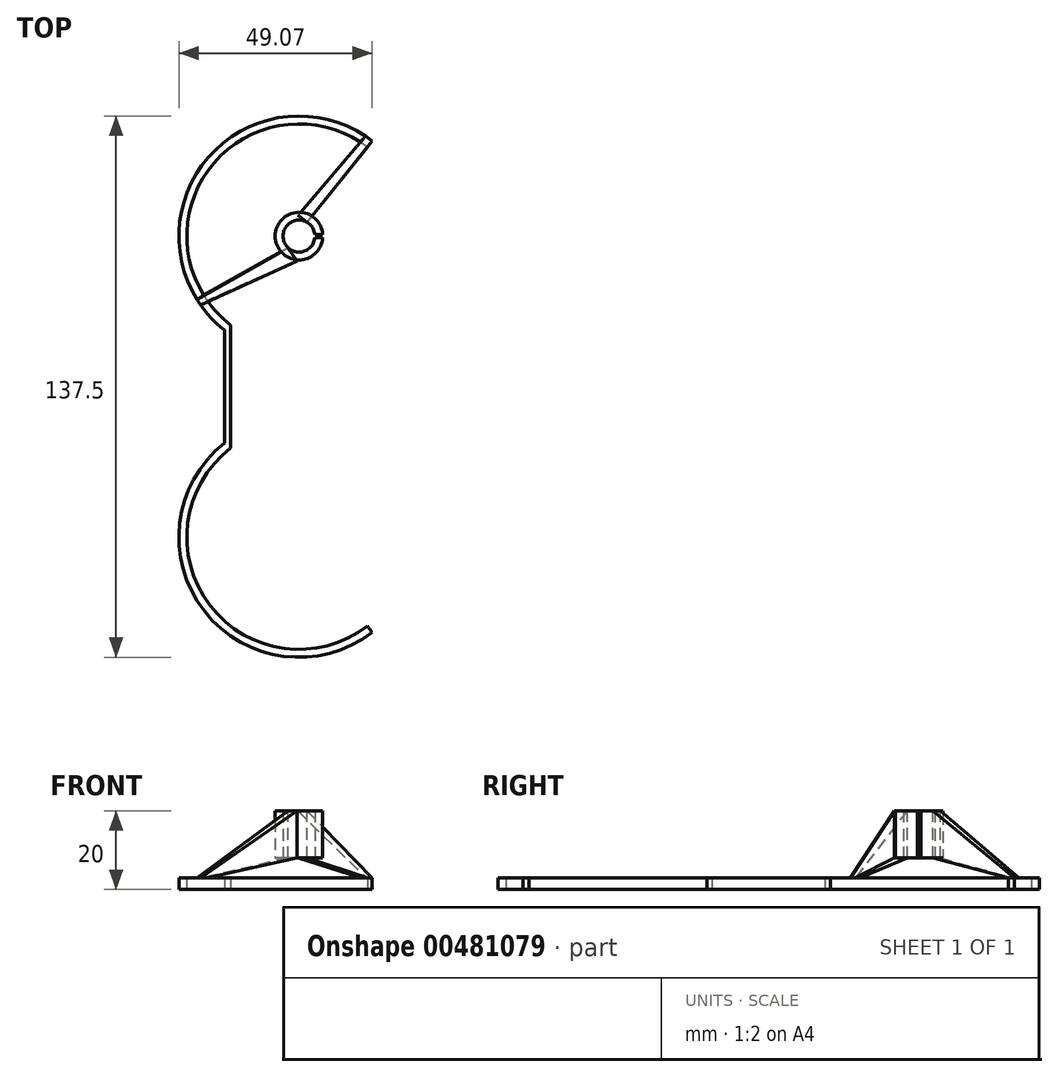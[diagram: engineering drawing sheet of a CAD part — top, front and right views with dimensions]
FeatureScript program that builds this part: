
annotation { "Feature Type Name" : "Feature", "Feature Type Description" : "" }
export const myFeature = defineFeature(function(context is Context, id is Id, definition is map)
    precondition{}
    {
        {
            var Q0;
            Q0=qCreatedBy(makeId("Top.planeOp"),FACE);
            var sketch = newSketch(context, id + "F0", { "sketchPlane" : qUnion([Q0])});
            skPoint(sketch, "E0.MirrorP", {"position": v(0, -38.25) * mm});
            skCircle(sketch, "E1", {"center": v(0, 38.25) * mm, "radius": 28.5 * mm});
            skLineSegment(sketch, "E2", {"start": v(0, 38.25) * mm, "end": v(45.61, 38.25) * mm, "construction": true});
            skCircle(sketch, "E3", {"center": v(0, 38.25) * mm, "radius": 30.5 * mm});
            skLineSegment(sketch, "E4", {"start": v(0, 38.25) * mm, "end": v(-46.13, 38.25) * mm, "construction": true});
            skLineSegment(sketch, "E5.left", {"start": v(-18.95, 14.35) * mm, "end": v(-18.95, 0) * mm});
            skLineSegment(sketch, "E5.right", {"start": v(-17.35, 13.17) * mm, "end": v(-17.35, 0) * mm});
            skLineSegment(sketch, "E6", {"start": v(-18.95, 0) * mm, "end": v(-17.35, 0) * mm});
            skLineSegment(sketch, "E7", {"start": v(-17.35, 15.64) * mm, "end": v(-17.35, 13.17) * mm});
            skLineSegment(sketch, "E8", {"start": v(-17.35, 15.64) * mm, "end": v(18.57, 62.45) * mm, "construction": true});
            skLineSegment(sketch, "E9", {"start": v(17.35, 60.86) * mm, "end": v(18.57, 62.45) * mm});
            skLineSegment(sketch, "E10", {"start": v(-24.98, 20.76) * mm, "end": v(0, 38.25) * mm, "construction": true});
            skSolve(sketch);
        }
        {
            var Q0;
            {var subQ0=sQuery(id+"F0.wireOp",EDGE,"E7");Q0=makeQuery(id+"F0.imprint","IMPRINT",FACE,{"disambiguationData":[TD([[makeQuery(id+"F0.imprint","IMPRINT",EDGE,{"derivedFrom":subQ0}),-1.0]])]});}
            var Q1;
            {var subQ0=sQuery(id+"F0.wireOp",EDGE,"E5.left");Q1=makeQuery(id+"F0.imprint","IMPRINT",FACE,{"disambiguationData":[TD([[makeQuery(id+"F0.imprint","IMPRINT",EDGE,{"derivedFrom":subQ0}),1.0]])]});}
            extrude(context, id + "F1", {"entities" : qUnion([Q0, Q1]), "offsetDistance" : 25 * mm, "depth" : 3 * mm});
        }
        {
            var Q0;
            Q0=makeQuery(id+"F1.opExtrude","CAP_FACE",FACE,{"disambiguationData":[OSD([sQuery(id+"F0.wireOp",EDGE,"E1"),sQuery(id+"F0.wireOp",EDGE,"E3"),sQuery(id+"F0.wireOp",EDGE,"E5.left"),sQuery(id+"F0.wireOp",EDGE,"E5.right"),sQuery(id+"F0.wireOp",EDGE,"E6"),sQuery(id+"F0.wireOp",EDGE,"E7"),sQuery(id+"F0.wireOp",EDGE,"E9")])],"isStart":false});
            cPlane(context, id + "F2", {"entities" : qUnion([Q0]), "cplaneType" : CPlaneType.OFFSET, "offset" : 5 * mm, "width" : 150 * mm, "height" : 150 * mm});
        }
        {
            var Q0;
            Q0=qCreatedBy(id+"F2.planeOp",FACE);
            var sketch = newSketch(context, id + "F3", { "sketchPlane" : qUnion([Q0])});
            skCircle(sketch, "E11", {"center": v(0, 38.25) * mm, "radius": 4.05 * mm});
            skCircle(sketch, "E12", {"center": v(0, 38.25) * mm, "radius": 6.05 * mm});
            skLineSegment(sketch, "E13.bottom", {"start": v(4.03, 37.85) * mm, "end": v(6.05, 37.85) * mm});
            skLineSegment(sketch, "E13.top", {"start": v(4.03, 38.65) * mm, "end": v(6.05, 38.65) * mm});
            skLineSegment(sketch, "E13.left", {"start": v(4.03, 37.85) * mm, "end": v(4.03, 38.65) * mm});
            skLineSegment(sketch, "E13.right", {"start": v(6.05, 37.85) * mm, "end": v(6.05, 38.65) * mm});
            skPoint(sketch, "E13.middle", {"position": v(5.04, 38.25) * mm});
            skLineSegment(sketch, "E14", {"start": v(-4.96, 34.78) * mm, "end": v(-3.32, 35.93) * mm, "construction": true});
            skLineSegment(sketch, "E15", {"start": v(2.47, 41.46) * mm, "end": v(3.68, 43.05) * mm, "construction": true});
            skLineSegment(sketch, "E16", {"start": v(-6.78, 40.88) * mm, "end": v(0.15, 30.98) * mm, "construction": true});
            skLineSegment(sketch, "E17", {"start": v(-1.22, 44.29) * mm, "end": v(6.15, 38.64) * mm, "construction": true});
            skSolve(sketch);
        }
        {
            var Q0;
            {var subQ4=sQuery(id+"F3.wireOp",EDGE,"E13.top");var subQ6=sQuery(id+"F3.wireOp",EDGE,"E12");var subQ8=makeQuery(id+"F3.imprint","INTERSECT",VERTEX,{"derivedFrom":[subQ6,subQ4]});Q0=makeQuery(id+"F3.imprint","IMPRINT",FACE,{"disambiguationData":[TD([[makeQuery(id+"F3.imprint","IMPRINT",EDGE,{"disambiguationData":[TD([[subQ8,-1.0]])],"derivedFrom":subQ6}),1.0]])]});}
            extrude(context, id + "F4", {"entities" : qUnion([Q0]), "depth" : 12 * mm, "offsetDistance" : 25 * mm});
        }
        {
            var Q0;
            Q0=makeQuery(id+"F1.opExtrude","CAP_FACE",FACE,{"disambiguationData":[OSD([sQuery(id+"F0.wireOp",EDGE,"E1"),sQuery(id+"F0.wireOp",EDGE,"E3"),sQuery(id+"F0.wireOp",EDGE,"E5.left"),sQuery(id+"F0.wireOp",EDGE,"E5.right"),sQuery(id+"F0.wireOp",EDGE,"E6"),sQuery(id+"F0.wireOp",EDGE,"E7"),sQuery(id+"F0.wireOp",EDGE,"E9")])],"isStart":false});
            var sketch = newSketch(context, id + "F5", { "sketchPlane" : qUnion([Q0])});
            skLineSegment(sketch, "E18", {"start": v(-25.87, 22.1) * mm, "end": v(-24.23, 23.24) * mm});
            skLineSegment(sketch, "E19", {"start": v(-24.98, 20.76) * mm, "end": v(-23.35, 21.9) * mm});
            skLineSegment(sketch, "E20", {"start": v(16.94, 63.61) * mm, "end": v(15.72, 62.02) * mm});
            skSolve(sketch);
        }
        {
            var Q0;
            Q0=sQuery(id+"F3.wireOp",EDGE,"E16");
            cPlane(context, id + "F6", {"entities" : qUnion([Q0]), "cplaneType" : CPlaneType.LINE_ANGLE, "offset" : 25 * mm, "angle" : 90 * degree, "width" : 150 * mm, "height" : 150 * mm});
        }
        {
            var Q0;
            Q0=qCreatedBy(id+"F6.planeOp",FACE);
            var sketch = newSketch(context, id + "F7", { "sketchPlane" : qUnion([Q0])});
            skLineSegment(sketch, "E21.bottom", {"start": v(30.48, 8) * mm, "end": v(26.48, 8) * mm});
            skLineSegment(sketch, "E21.top", {"start": v(30.48, 20) * mm, "end": v(26.48, 20) * mm});
            skLineSegment(sketch, "E21.left", {"start": v(30.48, 8) * mm, "end": v(30.48, 20) * mm});
            skLineSegment(sketch, "E21.right", {"start": v(26.48, 8) * mm, "end": v(26.48, 20) * mm});
            skSolve(sketch);
        }
        {
            var Q0;
            Q0 = qSketchRegion(id + "F7", true);
            var Q1;
            {var subQ0=sQuery(id+"F5.wireOp",EDGE,"E18");Q1=makeQuery(id+"F5.imprint","IMPRINT",FACE,{"disambiguationData":[TD([[makeQuery(id+"F5.imprint","IMPRINT",EDGE,{"derivedFrom":subQ0}),-1.0]])]});}
            loft(context, id + "F8", {"sheetProfilesArray" : [{ "sheetProfileEntities" : qUnion([Q0]) }, { "sheetProfileEntities" : qUnion([Q1]) }]});
        }
        {
            var Q0;
            Q0=sQuery(id+"F3.wireOp",EDGE,"E17");
            cPlane(context, id + "F9", {"entities" : qUnion([Q0]), "cplaneType" : CPlaneType.LINE_ANGLE, "offset" : 25 * mm, "angle" : 0 * degree, "width" : 150 * mm, "height" : 150 * mm});
        }
        {
            var Q0;
            Q0=qCreatedBy(id+"F9.planeOp",FACE);
            var sketch = newSketch(context, id + "F10", { "sketchPlane" : qUnion([Q0])});
            skLineSegment(sketch, "E22.bottom", {"start": v(26.75, 8) * mm, "end": v(23.75, 8) * mm});
            skLineSegment(sketch, "E22.top", {"start": v(26.75, 20) * mm, "end": v(23.75, 20) * mm});
            skLineSegment(sketch, "E22.left", {"start": v(26.75, 8) * mm, "end": v(26.75, 20) * mm});
            skLineSegment(sketch, "E22.right", {"start": v(23.75, 8) * mm, "end": v(23.75, 20) * mm});
            skSolve(sketch);
        }
        {
            var Q0;
            Q0 = qSketchRegion(id + "F10", true);
            var Q1;
            {var subQ0=sQuery(id+"F5.wireOp",EDGE,"E20");Q1=makeQuery(id+"F5.imprint","IMPRINT",FACE,{"disambiguationData":[TD([[makeQuery(id+"F5.imprint","IMPRINT",EDGE,{"derivedFrom":subQ0}),1.0]])]});}
            loft(context, id + "F11", {"sheetProfilesArray" : [{ "sheetProfileEntities" : qUnion([Q0]) }, { "sheetProfileEntities" : qUnion([Q1]) }]});
        }
        {
            var Q0;
            Q0=makeQuery(id+"F1.opExtrude","SWEPT_BODY",BODY,{"disambiguationData":[OSD([sQuery(id+"F0.wireOp",EDGE,"ddY038Ko-QcGd-95kh-qWaL-JcS8UjDePdMG"),sQuery(id+"F0.wireOp",EDGE,"GqMhPdvA-aU3g-5EOh-kGEM-E9VfKXcgTchY"),sQuery(id+"F0.wireOp",EDGE,"E1"),sQuery(id+"F0.wireOp",EDGE,"E3"),sQuery(id+"F0.wireOp",EDGE,"aLqe13To-ENuk-Plb5-EUUH-spIAvATz8cka"),sQuery(id+"F0.wireOp",EDGE,"iNK39r5I-N8Kh-ghXa-SgdF-1P0qzHFAxhFD"),sQuery(id+"F0.wireOp",EDGE,"zehJDxNT-YYuY-av34-19fy-jMS9ZvFWVtcO"),sQuery(id+"F0.wireOp",EDGE,"GhgDo7KD-Vc9L-K850-kRqi-BM5ShqcGHkGh"),sQuery(id+"F0.wireOp",EDGE,"881b5292-010a-4c1d-b706-68c4c8cc73aa0.MirrorCS"),sQuery(id+"F0.wireOp",EDGE,"ac8275d0-5f08-4727-a553-10be3d09fafa0.MirrorCS"),sQuery(id+"F0.wireOp",EDGE,"E5.top"),sQuery(id+"F0.wireOp",EDGE,"E5.left"),sQuery(id+"F0.wireOp",EDGE,"E5.right")])]});
            var Q1;
            Q1=qCreatedBy(makeId("Front.planeOp"),FACE);
            mirror(context, id + "F12", {"operationType" : NewBodyOperationType.ADD, "entities" : qUnion([Q0]), "mirrorPlane" : qUnion([Q1])});
        }
    });
